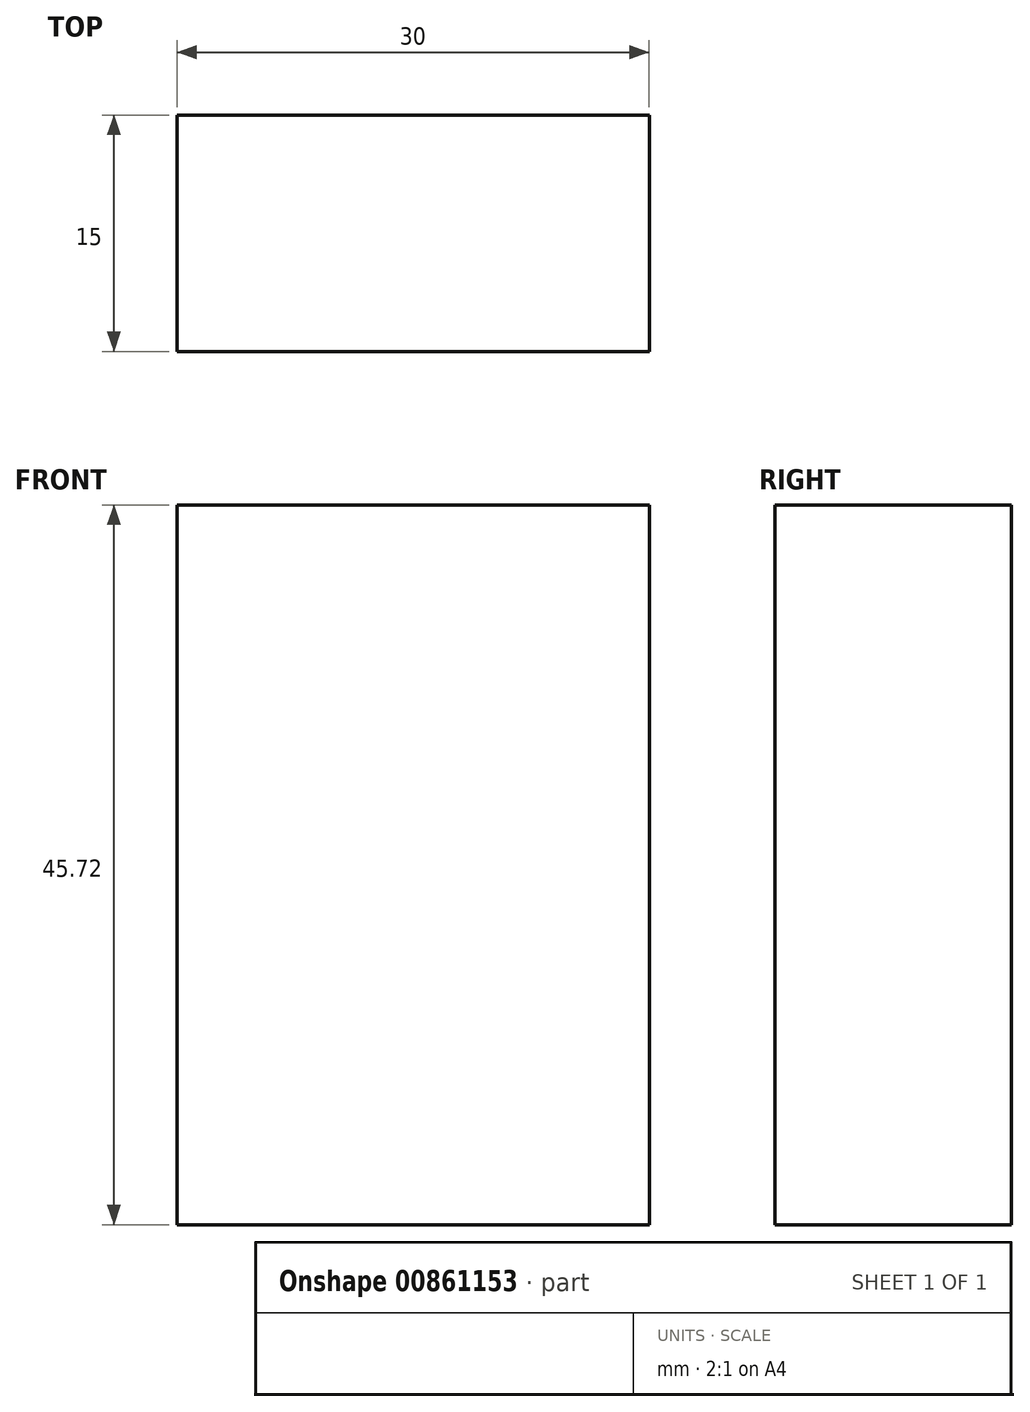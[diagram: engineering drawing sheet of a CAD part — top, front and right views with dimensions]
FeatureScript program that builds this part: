
annotation { "Feature Type Name" : "Feature", "Feature Type Description" : "" }
export const myFeature = defineFeature(function(context is Context, id is Id, definition is map)
    precondition{}
    {
        {
            var Q0;
            Q0=qCreatedBy(makeId("Top.planeOp"),FACE);
            var sketch = newSketch(context, id + "F0", { "sketchPlane" : qUnion([Q0])});
            skLineSegment(sketch, "E0.bottom", {"start": v(-19.58, 25.37) * mm, "end": v(10.42, 25.37) * mm});
            skLineSegment(sketch, "E0.top", {"start": v(-19.58, 10.37) * mm, "end": v(10.42, 10.37) * mm});
            skLineSegment(sketch, "E0.left", {"start": v(-19.58, 25.37) * mm, "end": v(-19.58, 10.37) * mm});
            skLineSegment(sketch, "E0.right", {"start": v(10.42, 25.37) * mm, "end": v(10.42, 10.37) * mm});
            skSolve(sketch);
        }
        {
            var Q0;
            Q0=makeQuery(id+"F0.imprint","IMPRINT",FACE,{"disambiguationData":[TD([[makeQuery(id+"F0.imprint","IMPRINT",EDGE,{"derivedFrom":sQuery(id+"F0.wireOp",EDGE,"E0.bottom")}),-1.0]])]});
            extrude(context, id + "F1", {"entities" : qUnion([Q0]), "depth" : 45.72 * mm, "offsetDistance" : 25 * mm});
        }
    });
